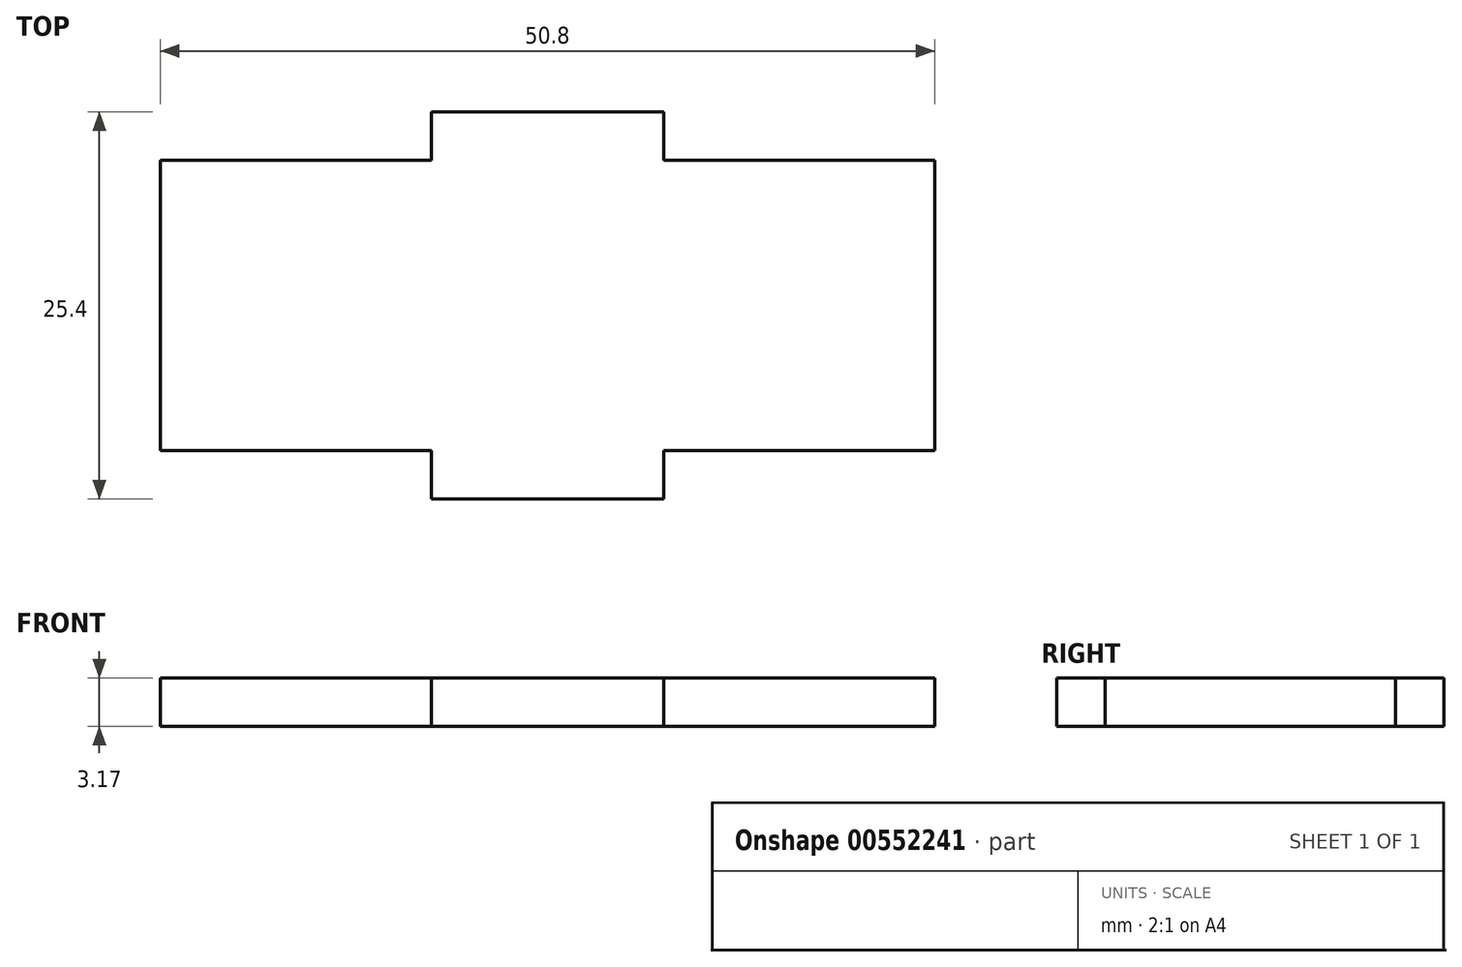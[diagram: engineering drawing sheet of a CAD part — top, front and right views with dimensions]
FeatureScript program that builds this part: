
annotation { "Feature Type Name" : "Feature", "Feature Type Description" : "" }
export const myFeature = defineFeature(function(context is Context, id is Id, definition is map)
    precondition{}
    {
        {
            var Q0;
            Q0=qCreatedBy(makeId("Top.planeOp"),FACE);
            var sketch = newSketch(context, id + "F0", { "sketchPlane" : qUnion([Q0])});
            skPoint(sketch, "E0.middle", {"position": v(0, 0) * mm});
            skLineSegment(sketch, "E1", {"start": v(7.2, -12.08) * mm, "end": v(-8.04, -12.08) * mm});
            skLineSegment(sketch, "E2", {"start": v(-8.04, -12.08) * mm, "end": v(-8.04, -8.9) * mm});
            skLineSegment(sketch, "E3", {"start": v(7.2, -12.08) * mm, "end": v(7.2, -8.9) * mm});
            skLineSegment(sketch, "E4", {"start": v(24.98, 6.97) * mm, "end": v(24.98, -5.73) * mm});
            skLineSegment(sketch, "E5", {"start": v(7.2, 13.32) * mm, "end": v(-8.04, 13.32) * mm});
            skLineSegment(sketch, "E6", {"start": v(-25.82, 6.97) * mm, "end": v(-25.82, -5.73) * mm});
            skLineSegment(sketch, "E7", {"start": v(24.98, -5.73) * mm, "end": v(24.98, -8.9) * mm});
            skLineSegment(sketch, "E8", {"start": v(24.98, -8.9) * mm, "end": v(7.2, -8.9) * mm});
            skLineSegment(sketch, "E9", {"start": v(-8.04, -8.9) * mm, "end": v(-25.82, -8.9) * mm});
            skLineSegment(sketch, "E10", {"start": v(-25.82, -8.9) * mm, "end": v(-25.82, -5.73) * mm});
            skLineSegment(sketch, "E11", {"start": v(24.98, 6.97) * mm, "end": v(24.98, 10.14) * mm});
            skLineSegment(sketch, "E12", {"start": v(24.98, 10.14) * mm, "end": v(7.2, 10.14) * mm});
            skLineSegment(sketch, "E13", {"start": v(-25.82, 6.97) * mm, "end": v(-25.82, 10.14) * mm});
            skLineSegment(sketch, "E14", {"start": v(-25.82, 10.14) * mm, "end": v(-8.04, 10.14) * mm});
            skLineSegment(sketch, "E15", {"start": v(7.2, 13.32) * mm, "end": v(7.2, 10.14) * mm});
            skLineSegment(sketch, "E16", {"start": v(-8.04, 13.32) * mm, "end": v(-8.04, 10.14) * mm});
            skSolve(sketch);
        }
        {
            var Q0;
            Q0 = qSketchRegion(id + "F0", true);
            extrude(context, id + "F1", {"entities" : qUnion([Q0]), "depth" : 3.17 * mm, "offsetDistance" : 25.4 * mm});
        }
    });
